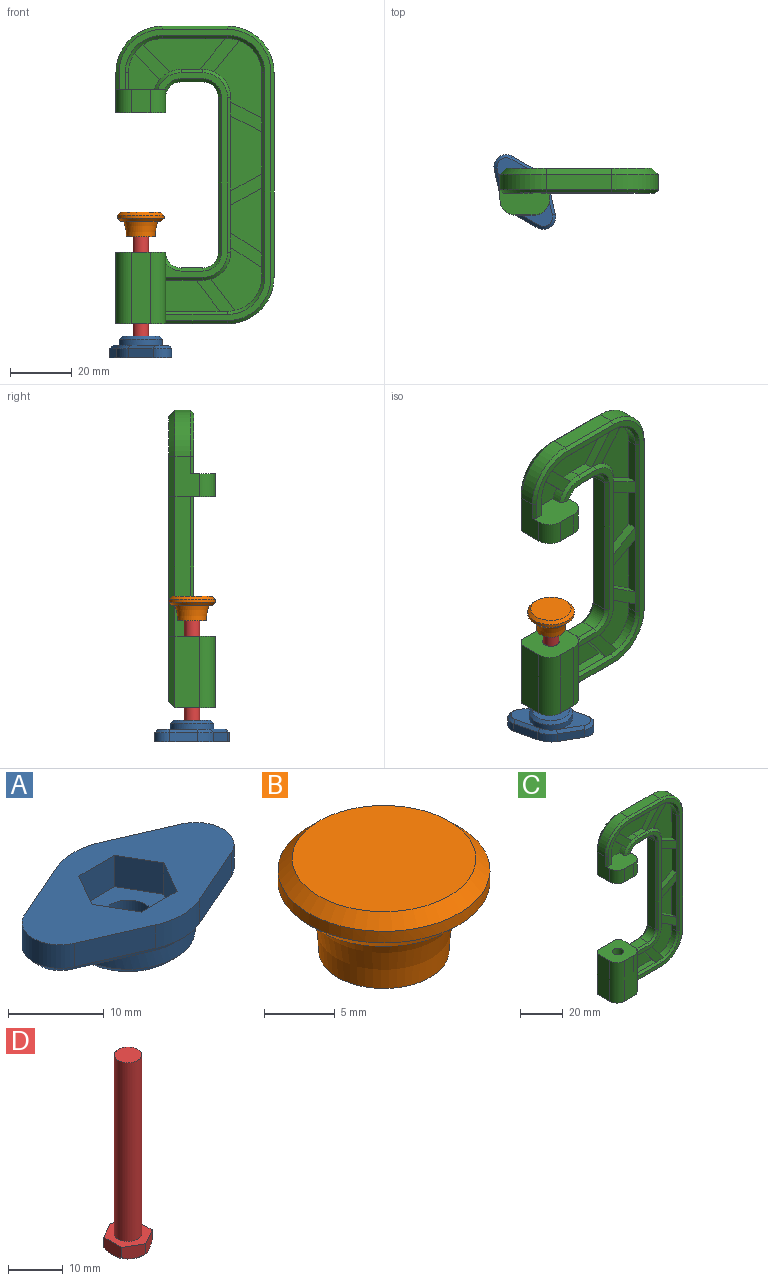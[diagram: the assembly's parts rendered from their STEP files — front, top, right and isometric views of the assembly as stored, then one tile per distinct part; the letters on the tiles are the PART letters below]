
ASSEMBLY  parts=4 mates=3
PART A: 30 faces, bbox 28x16x7 mm
  f0: plane 12.83x10.2mm, normal (0,0,-1), area 45.3mm2, adj f12,f24,f26,f28
  f1: cylinder r=2.65mm len=5.3mm, axis (0,0,1), area 50mm2, adj f13,f14
  f2: cylinder r=4mm len=7.33mm, axis (0,0,-1), area 27.8mm2, adj f3,f5,f7,f23
  f3: plane 8.4x3.67mm, normal (0.4,0.92,0), area 27.5mm2, adj f2,f4,f5,f21
  f4: cylinder r=8mm len=6.4mm, axis (0,0,-1), area 19.8mm2, adj f3,f5,f10,f22
  f5: plane 28x16mm, normal (0,0,1), area 236.4mm2, adj f2,f3,f4,f7,f8,f9,f10,f11
  f6: plane 12.83x10.2mm, normal (0,0,-1), area 45.3mm2, adj f12,f21,f23,f25
  f7: plane 8.4x3.67mm, normal (0.4,-0.92,0), area 27.5mm2, adj f2,f5,f8,f25
  f8: cylinder r=8mm len=6.4mm, axis (0,0,-1), area 19.8mm2, adj f5,f7,f11,f27
  f9: cylinder r=4mm len=7.33mm, axis (0,0,-1), area 27.8mm2, adj f5,f10,f11,f26
  f10: plane 8.4x3.67mm, normal (-0.4,0.92,0), area 27.5mm2, adj f4,f5,f9,f24
  f11: plane 8.4x3.67mm, normal (-0.4,-0.92,0), area 27.5mm2, adj f5,f8,f9,f28
  f12: cylinder r=7mm len=14mm, axis (0,0,1), area 88mm2, adj f0,f6,f22,f27,f29
  f13: plane 12x12mm, normal (0,0,-1), area 91mm2, adj f1,f29
  f14: plane 10.62x9.2mm, normal (0,0,1), area 51.2mm2, adj f1,f15,f16,f17,f18,f19,f20
  f15: plane 5.31x4mm, normal (0,1,0), area 21.2mm2, adj f5,f14,f16,f20
  f16: plane 4.6x4mm, normal (-0.87,0.5,0), area 21.2mm2, adj f5,f14,f15,f17
  f17: plane 4.6x4mm, normal (-0.87,-0.5,0), area 21.2mm2, adj f5,f14,f16,f18
  f18: plane 5.31x4mm, normal (0,-1,0), area 21.2mm2, adj f5,f14,f17,f19
  f19: plane 4.6x4mm, normal (0.87,-0.5,0), area 21.2mm2, adj f5,f14,f18,f20
  f20: plane 4.6x4mm, normal (0.87,0.5,0), area 21.2mm2, adj f5,f14,f15,f19
  f21: plane 8.8x4.58mm, normal (0.28,0.65,-0.71), area 13mm2, adj f3,f6,f22,f23
  f22: cone r=8mm half-angle=45deg, axis (0,0,1), area 8.7mm2, adj f4,f12,f21,f24
  f23: cone r=4mm half-angle=45deg, axis (0,0,1), area 11.5mm2, adj f2,f6,f21,f25
  f24: plane 8.8x4.58mm, normal (-0.28,0.65,-0.71), area 13mm2, adj f0,f10,f22,f26
  f25: plane 8.8x4.58mm, normal (0.28,-0.65,-0.71), area 13mm2, adj f6,f7,f23,f27
  f26: cone r=3mm half-angle=45deg, axis (0,0,1), area 11.5mm2, adj f0,f9,f24,f28
  f27: cone r=7mm half-angle=45deg, axis (0,0,1), area 8.7mm2, adj f8,f12,f25,f28
  f28: plane 8.8x4.58mm, normal (-0.28,-0.65,-0.71), area 13mm2, adj f0,f11,f26,f27
  f29: cone r=6mm half-angle=45deg, axis (0,0,1), area 57.8mm2, adj f12,f13
PART B: 10 faces, bbox 19x19x20.4 mm
  f0: plane 13x13mm, normal (0,0,1), area 132.7mm2, adj f8
  f1: plane 5.2x5.2mm, normal (0,0,-1), area 21.2mm2, adj f2
  f2: cylinder r=2.6mm len=5.2mm, axis (0,0,-1), area 49mm2, adj f1,f9
  f3: plane 9.2x9.2mm, normal (0,0,-1), area 36.3mm2, adj f4,f9
  f4: torus R=18.94mm, axis (0,0,-1), area 157.3mm2, adj f3,f5
  f5: plane 13x13mm, normal (0,0,-1), area 37.7mm2, adj f4,f7
  f6: cylinder r=7.5mm len=15mm, axis (0,0,-1), area 47.1mm2, adj f7,f8
  f7: cone r=6.5mm half-angle=45deg, axis (0,0,1), area 62.2mm2, adj f5,f6
  f8: cone r=7.5mm half-angle=45deg, axis (0,0,-1), area 62.2mm2, adj f0,f6
  f9: cone r=2.6mm half-angle=14deg, axis (0,0,-1), area 36.9mm2, adj f2,f3
PART C: 119 faces, bbox 51x15x96 mm
  f0: plane 16x15mm, normal (0,0,1), area 203.2mm2, adj f9,f34,f42,f45,f47,f69,f104,f107
  f1: plane 3.09x3mm, normal (-1,0,0), area 9.3mm2, adj f15,f17,f64,f96
  f2: plane 20.86x3mm, normal (-1,0,0), area 62.6mm2, adj f18,f61,f63,f96
  f3: plane 13.71x3mm, normal (-1,0,0), area 41.1mm2, adj f20,f54,f60,f96
  f4: plane 3x1.56mm, normal (1,0,0), area 4.7mm2, adj f24,f26,f55,f89
  f5: plane 24.16x3mm, normal (1,0,0), area 72.5mm2, adj f20,f54,f60,f89
  f6: plane 8.88x3mm, normal (1,0,0), area 26.6mm2, adj f18,f61,f63,f89
  f7: cylinder r=11mm len=6.32mm, axis (0,-1,0), area 20.2mm2, adj f21,f40,f57,f93
  f8: cylinder r=9mm len=3.36mm, axis (0,-1,0), area 11.5mm2, adj f14,f58,f70,f86
  f9: cylinder r=2.65mm len=23mm, axis (0,0,-1), area 383mm2, adj f0,f44
  f10: cylinder r=9mm len=3.57mm, axis (0,-1,0), area 11mm2, adj f21,f41,f57,f86
  f11: plane 94x49mm, normal (0,-1,0), area 347.5mm2, adj f42,f70,f79,f80,f81,f82,f83,f84
  f12: plane 66x22.6mm, normal (0,-1,0), area 202.8mm2, adj f42,f70,f72,f73,f74,f75,f76,f77
  f13: plane 5.5x3mm, normal (1,0,0), area 16.5mm2, adj f14,f22,f70,f92
  f14: plane 11.65x10.17mm, normal (0,-1,0), area 76.8mm2, adj f8,f13,f22,f58,f70
  f15: plane 20.34x16.34mm, normal (0,-1,0), area 186.9mm2, adj f1,f17,f19,f50,f64,f66
  f16: plane 9.94x3mm, normal (0,0,-1), area 29.8mm2, adj f23,f42,f67,f91
  f17: cylinder r=11mm len=10.74mm, axis (0,-1,0), area 44.6mm2, adj f1,f15,f66,f97
  f18: plane 20.86x10mm, normal (0,-1,0), area 148.7mm2, adj f2,f6,f61,f63
  f19: plane 3x1.61mm, normal (1,0,0), area 4.8mm2, adj f15,f50,f64,f89
  f20: plane 24.16x10mm, normal (0,-1,0), area 189.4mm2, adj f3,f5,f54,f60
  f21: plane 26.57x10.74mm, normal (0,-1,0), area 189.8mm2, adj f7,f10,f40,f41,f52,f57
  f22: cylinder r=11mm len=6.15mm, axis (0,-1,0), area 19.6mm2, adj f13,f14,f58,f93
  f23: plane 17.57x10mm, normal (0,-1,0), area 137.5mm2, adj f16,f42,f49,f67
  f24: plane 24.84x15.39mm, normal (0,-1,0), area 228.6mm2, adj f4,f25,f26,f39,f51,f55
  f25: cylinder r=11mm len=10.3mm, axis (0,-1,0), area 40mm2, adj f24,f39,f51,f95
  f26: cylinder r=9mm len=8.24mm, axis (0,-1,0), area 31.3mm2, adj f4,f24,f51,f88
  f27: plane 16x15mm, normal (0,0,-1), area 225.3mm2, adj f28,f33,f34,f71,f99,f114,f115,f116
  f28: plane 8x7.5mm, normal (1,0,0), area 47mm2, adj f27,f37,f70,f78,f114,f115
  f29: plane 7x5mm, normal (0,0,-1), area 35mm2, adj f37,f38,f77,f112
  f30: plane 50x5mm, normal (-1,0,0), area 250mm2, adj f38,f48,f75,f110
  f31: plane 66x5mm, normal (1,0,0), area 330mm2, adj f35,f46,f83,f103
  f32: plane 21x5mm, normal (0,0,1), area 105mm2, adj f35,f36,f81,f101
  f33: plane 13x8mm, normal (-1,0,0), area 87.5mm2, adj f27,f36,f70,f79,f99,f116
  f34: plane 92x47mm, normal (0,1,0), area 2373.3mm2, adj f0,f27,f99,f100,f101,f102,f103,f104
  f35: cylinder r=15mm len=15mm, axis (0,1,0), area 117.8mm2, adj f31,f32,f82,f102
  f36: cylinder r=15mm len=15mm, axis (0,1,0), area 117.8mm2, adj f32,f33,f80,f100
  f37: cylinder r=5mm len=5mm, axis (0,-1,0), area 39.3mm2, adj f28,f29,f78,f113
  f38: cylinder r=5mm len=5mm, axis (0,-1,0), area 39.3mm2, adj f29,f30,f76,f111
  f39: plane 14.54x3mm, normal (-1,0,0), area 43.6mm2, adj f24,f25,f55,f96
  f40: plane 20.25x3mm, normal (0,0,-1), area 60.8mm2, adj f7,f21,f52,f94
  f41: plane 6.06x3mm, normal (0,0,1), area 18.2mm2, adj f10,f21,f52,f87
  f42: plane 23x6mm, normal (1,0,0), area 89.7mm2, adj f0,f11,f12,f16,f23,f44,f49,f72
  f43: plane 7x5mm, normal (0,0,1), area 35mm2, adj f47,f48,f73,f108
  f44: plane 36x13mm, normal (0,0,-1), area 275.2mm2, adj f9,f42,f45,f46,f69,f85,f106,f117
  f45: plane 23x8mm, normal (-1,0,0), area 184mm2, adj f0,f44,f104,f118
  f46: cylinder r=15mm len=15mm, axis (0,1,0), area 117.8mm2, adj f31,f44,f84,f105
  f47: cylinder r=5mm len=5mm, axis (0,-1,0), area 39.3mm2, adj f0,f43,f72,f107
  f48: cylinder r=5mm len=5mm, axis (0,-1,0), area 39.3mm2, adj f30,f43,f74,f109
  f49: plane 17.57x3mm, normal (0,0,1), area 52.7mm2, adj f23,f42,f67,f98
  f50: cylinder r=9mm len=8.6mm, axis (0,-1,0), area 34.3mm2, adj f15,f19,f66,f90
  f51: plane 10.06x8.24mm, normal (0.77,0,-0.63), area 39mm2, adj f24,f25,f26,f53
  f52: plane 10x8.19mm, normal (-0.77,0,0.63), area 38.8mm2, adj f21,f40,f41,f53
  f53: plane 12.79x10.76mm, normal (0,-1,0), area 51.8mm2, adj f51,f52,f87,f88,f94,f95
  f54: plane 10x4.98mm, normal (-0.45,0,-0.89), area 33.5mm2, adj f3,f5,f20,f56
  f55: plane 10x4.98mm, normal (0.45,0,0.89), area 33.5mm2, adj f4,f24,f39,f56
  f56: plane 10x9.45mm, normal (0,-1,0), area 44.7mm2, adj f54,f55,f89,f96
  f57: plane 8.74x8.74mm, normal (0.71,0,0.71), area 37.1mm2, adj f7,f10,f21,f59
  f58: plane 8.29x8.29mm, normal (-0.71,0,-0.71), area 35.2mm2, adj f8,f14,f22,f59
  f59: plane 11.55x11.14mm, normal (0,-1,0), area 48mm2, adj f57,f58,f86,f93
  f60: plane 10x5.46mm, normal (-0.48,0,0.88), area 34.2mm2, adj f3,f5,f20,f62
  f61: plane 10x5.46mm, normal (0.48,0,-0.88), area 34.2mm2, adj f2,f6,f18,f62
  f62: plane 10.02x10mm, normal (0,-1,0), area 45.6mm2, adj f60,f61,f89,f96
  f63: plane 10x6.52mm, normal (0.55,0,0.84), area 35.8mm2, adj f2,f6,f18,f65
  f64: plane 10x6.52mm, normal (-0.55,0,-0.84), area 35.8mm2, adj f1,f15,f19,f65
  f65: plane 11.29x10mm, normal (0,-1,0), area 47.7mm2, adj f63,f64,f89,f96
  f66: plane 10.14x7.74mm, normal (0.79,0,0.61), area 38.3mm2, adj f15,f17,f50,f68
  f67: plane 10x7.63mm, normal (-0.79,0,-0.61), area 37.7mm2, adj f16,f23,f49,f68
  f68: plane 12.46x10.4mm, normal (0,-1,0), area 50.5mm2, adj f66,f67,f90,f91,f97,f98
  f69: plane 23x6mm, normal (0,-1,0), area 138mm2, adj f0,f44,f117,f118
  f70: plane 16.02x11.02mm, normal (0,0,1), area 136.3mm2, adj f8,f11,f12,f13,f14,f28,f33,f71
  f71: plane 7.5x6mm, normal (0,-1,0), area 45mm2, adj f27,f70,f115,f116
  f72: cone r=5mm half-angle=45deg, axis (0,-1,0), area 9mm2, adj f12,f42,f47,f73
  f73: plane 7x1mm, normal (0,-0.71,0.71), area 9.9mm2, adj f12,f43,f72,f74
  f74: cone r=5mm half-angle=45deg, axis (0,-1,0), area 12.2mm2, adj f12,f48,f73,f75
  f75: plane 50x1mm, normal (-0.71,-0.71,0), area 70.7mm2, adj f12,f30,f74,f76
  f76: cone r=6mm half-angle=45deg, axis (0,-1,0), area 12.2mm2, adj f12,f38,f75,f77
  f77: plane 7x1mm, normal (0,-0.71,-0.71), area 9.9mm2, adj f12,f29,f76,f78
  f78: cone r=6mm half-angle=45deg, axis (0,-1,0), area 9.3mm2, adj f12,f28,f37,f70,f77
  f79: plane 5.5x1mm, normal (-0.71,-0.71,0), area 7.8mm2, adj f11,f33,f70,f80
  f80: cone r=14mm half-angle=45deg, axis (0,1,0), area 32.2mm2, adj f11,f36,f79,f81
  f81: plane 21x1mm, normal (0,-0.71,0.71), area 29.7mm2, adj f11,f32,f80,f82
  f82: cone r=14mm half-angle=45deg, axis (0,1,0), area 32.2mm2, adj f11,f35,f81,f83
  f83: plane 66x1mm, normal (0.71,-0.71,0), area 93.3mm2, adj f11,f31,f82,f84
  f84: cone r=15mm half-angle=45deg, axis (0,1,0), area 32.2mm2, adj f11,f46,f83,f85
  f85: plane 20x1mm, normal (0,-0.71,-0.71), area 28.3mm2, adj f11,f42,f44,f84
  f86: cone r=9mm half-angle=45deg, axis (0,1,0), area 15.3mm2, adj f8,f10,f12,f59,f70,f87
  f87: plane 7x1mm, normal (0,-0.71,0.71), area 9.9mm2, adj f12,f41,f53,f86,f88
  f88: cone r=9mm half-angle=45deg, axis (0,1,0), area 18.9mm2, adj f12,f26,f53,f87,f89
  f89: plane 50x1mm, normal (0.71,-0.71,0), area 70.7mm2, adj f4,f5,f6,f12,f19,f56,f62,f65
  f90: cone r=8mm half-angle=45deg, axis (0,1,0), area 18.9mm2, adj f12,f50,f68,f89,f91
  f91: plane 12x1mm, normal (0,-0.71,-0.71), area 17mm2, adj f12,f16,f42,f68,f90
  f92: plane 5.5x1mm, normal (0.71,-0.71,0), area 7.8mm2, adj f11,f13,f70,f93
  f93: cone r=11mm half-angle=45deg, axis (0,-1,0), area 25.5mm2, adj f7,f11,f22,f59,f92,f94
  f94: plane 21x1mm, normal (0,-0.71,-0.71), area 29.7mm2, adj f11,f40,f53,f93,f95
  f95: cone r=11mm half-angle=45deg, axis (0,-1,0), area 25.5mm2, adj f11,f25,f53,f94,f96
  f96: plane 66x1mm, normal (-0.71,-0.71,0), area 93.3mm2, adj f1,f2,f3,f11,f39,f56,f62,f65
  f97: cone r=12mm half-angle=45deg, axis (0,-1,0), area 25.5mm2, adj f11,f17,f68,f96,f98
  f98: plane 20x1mm, normal (0,-0.71,0.71), area 28.3mm2, adj f11,f42,f49,f68,f97
  f99: plane 13x2mm, normal (-0.71,0.71,0), area 36.8mm2, adj f27,f33,f34,f100
  f100: cone r=13mm half-angle=45deg, axis (0,-1,0), area 62.2mm2, adj f34,f36,f99,f101
  f101: plane 21x2mm, normal (0,0.71,0.71), area 59.4mm2, adj f32,f34,f100,f102
  f102: cone r=13mm half-angle=45deg, axis (0,-1,0), area 62.2mm2, adj f34,f35,f101,f103
  f103: plane 66x2mm, normal (0.71,0.71,0), area 186.7mm2, adj f31,f34,f102,f105
  f104: plane 23x2mm, normal (-0.71,0.71,0), area 62.2mm2, adj f0,f34,f45,f106
  f105: cone r=15mm half-angle=45deg, axis (0,-1,0), area 62.2mm2, adj f34,f46,f103,f106
  f106: plane 36x2mm, normal (0,0.71,-0.71), area 99mm2, adj f34,f44,f104,f105
  f107: cone r=5mm half-angle=45deg, axis (0,1,0), area 26.7mm2, adj f0,f34,f47,f108
  f108: plane 7x2mm, normal (0,0.71,0.71), area 19.8mm2, adj f34,f43,f107,f109
  f109: cone r=5mm half-angle=45deg, axis (0,1,0), area 26.7mm2, adj f34,f48,f108,f110
  f110: plane 50x2mm, normal (-0.71,0.71,0), area 141.4mm2, adj f30,f34,f109,f111
  f111: cone r=7mm half-angle=45deg, axis (0,1,0), area 26.7mm2, adj f34,f38,f110,f112
  f112: plane 7x2mm, normal (0,0.71,-0.71), area 19.8mm2, adj f29,f34,f111,f113
  f113: cone r=7mm half-angle=45deg, axis (0,1,0), area 26.7mm2, adj f34,f37,f112,f114
  f114: plane 5x2mm, normal (0.71,0.71,0), area 14.1mm2, adj f27,f28,f34,f113
  f115: cylinder r=5mm len=7.5mm, axis (0,0,1), area 58.9mm2, adj f27,f28,f70,f71
  f116: cylinder r=5mm len=7.5mm, axis (0,0,-1), area 58.9mm2, adj f27,f33,f70,f71
  f117: cylinder r=5mm len=23mm, axis (0,0,-1), area 180.6mm2, adj f0,f42,f44,f69
  f118: cylinder r=5mm len=23mm, axis (0,0,1), area 180.6mm2, adj f0,f44,f45,f69
PART D: 11 faces, bbox 9.1x9.1x43 mm
  f0: plane 3.95x2.86mm, normal (-0.5,-0.87,0), area 12.1mm2, adj f1,f5,f6,f7
  f1: plane 3.95x2.86mm, normal (0.5,-0.87,0), area 12.1mm2, adj f0,f2,f6,f7
  f2: plane 4.57x2.86mm, normal (1,0,0), area 12.1mm2, adj f1,f3,f6,f7
  f3: plane 3.95x2.86mm, normal (0.5,0.87,0), area 12.1mm2, adj f2,f4,f6,f7
  f4: plane 3.95x2.86mm, normal (-0.5,0.87,0), area 12.1mm2, adj f3,f5,f6,f7
  f5: plane 4.57x2.86mm, normal (-1,0,0), area 12.1mm2, adj f0,f4,f6,f7
  f6: plane 9.12x7.9mm, normal (0,0,1), area 34.4mm2, adj f0,f1,f2,f3,f4,f5,f9
  f7: cone r=4.56mm half-angle=45deg, axis (0,0,1), area 12.2mm2, adj f0,f1,f2,f3,f4,f5,f8
  f8: plane 7.61x7.61mm, normal (0,0,-1), area 45.4mm2, adj f7
  f9: cylinder r=2.5mm len=40mm, axis (0,0,-1), area 628.3mm2, adj f6,f10
  f10: plane 5x5mm, normal (0,0,1), area 19.6mm2, adj f9
PLACE A rot(axis=(-0.45,-0.89,0),180deg) t=(22.94,4.69,-22.46)mm
PLACE B rot(axis=(0,0,1),36.5deg) t=(22.94,4.69,12.54)mm
PLACE C t=(22.94,12.19,32.54)mm fixed
PLACE D rot(axis=(0,0,1),36.5deg) t=(22.94,4.69,-22.46)mm
MATE fastened B.f2 <-> D.f9  axis (0,0,-1) through (22.94,4.69,17.54)mm
MATE fastened A.f1 <-> D.f9  axis (0,0,-1) through (22.94,4.69,-22.46)mm
MATE revolute D.f9 <-> C.f9  axis (0,0,-1) through (22.94,4.69,17.54)mm
